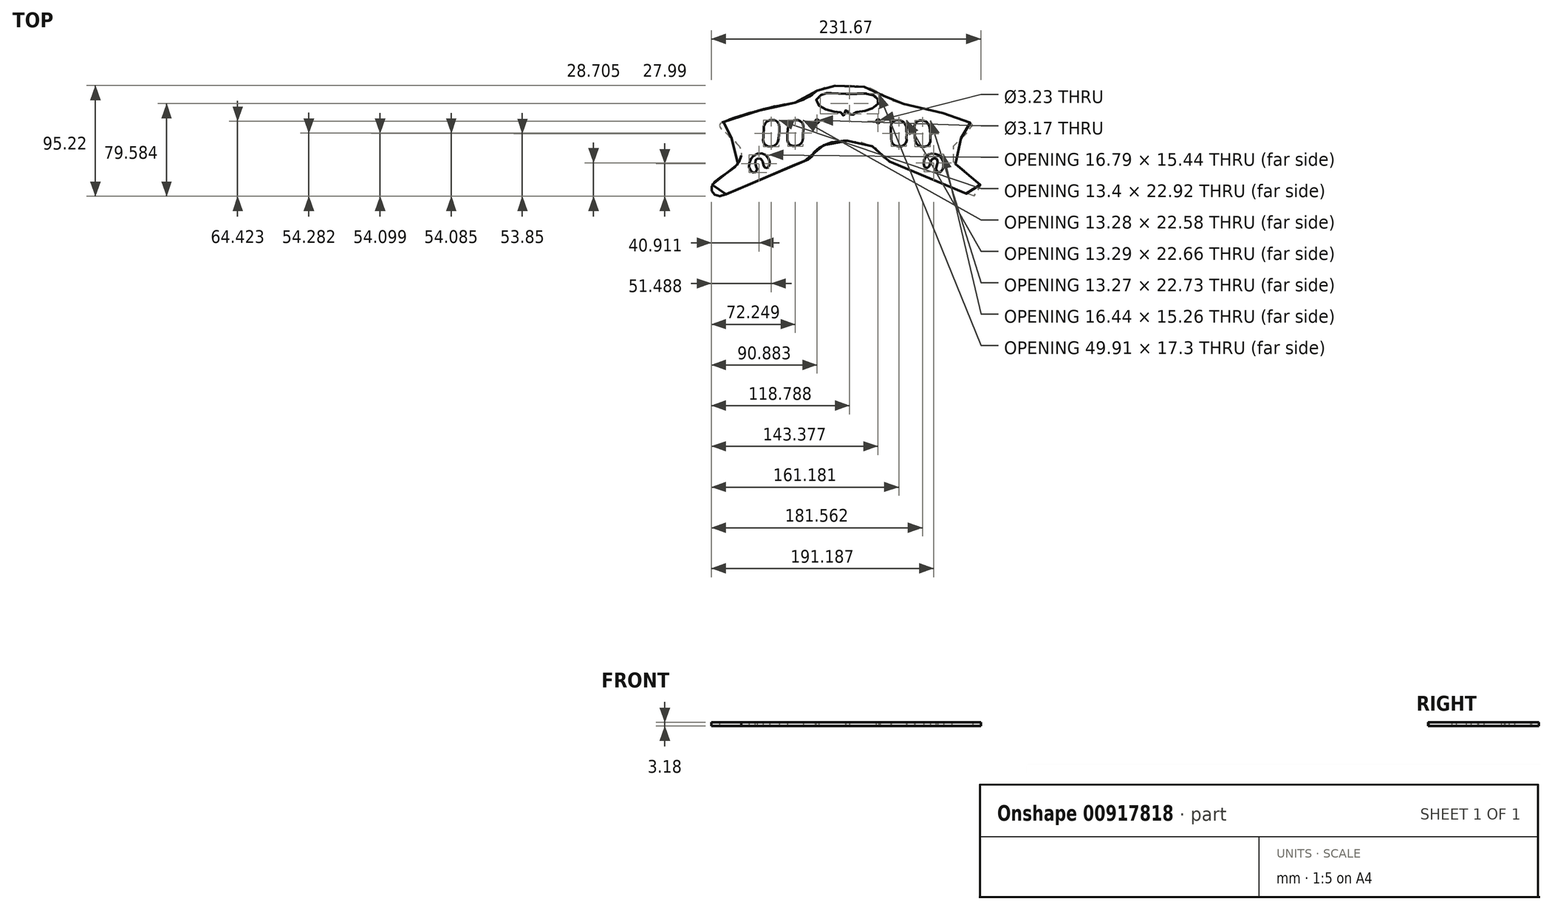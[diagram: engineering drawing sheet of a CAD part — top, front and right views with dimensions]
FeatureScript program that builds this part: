
annotation { "Feature Type Name" : "Feature", "Feature Type Description" : "" }
export const myFeature = defineFeature(function(context is Context, id is Id, definition is map)
    precondition{}
    {
        {
            var Q0;
            Q0=qCreatedBy(makeId("Top.planeOp"),FACE);
            var sketch = newSketch(context, id + "F0", { "sketchPlane" : qUnion([Q0])});
            skFitSpline(sketch, "E0", {"points": [v(0, -14.2) * mm, v(3.4, -14.29) * mm, v(7.2, -14.54) * mm, v(11.16, -15.12) * mm, v(15.2, -16.3) * mm, v(19.09, -17.8) * mm, v(22.72, -19.58) * mm, v(25.84, -21.68) * mm, v(28.12, -24.3) * mm, v(29.39, -26.82) * mm, v(30.57, -28.59) * mm, v(32.68, -30.36) * mm, v(36.14, -31.95) * mm, v(42.3, -34.56) * mm, v(100.55, -58.96) * mm, v(103.89, -60.5) * mm, v(106.63, -61.46) * mm, v(109.85, -61.22) * mm, v(112.23, -59.9) * mm, v(114.14, -57.16) * mm, v(114.5, -53.82) * mm, v(113.65, -50.84) * mm, v(111.5, -48.45) * mm, v(104.94, -43.46) * mm, v(98.14, -38.58) * mm, v(93.36, -34.89) * mm, v(90.61, -31.07) * mm, v(89.53, -25.7) * mm, v(90.24, -20.46) * mm, v(92.98, -16.17) * mm, v(97.5, -12.1) * mm, v(101.44, -8.64) * mm, v(104.36, -6.47) * mm, v(106.46, -4.36) * mm, v(107.76, -2.25) * mm, v(107.66, -0.65) * mm, v(106.94, 0.6) * mm, v(105.47, 1.38) * mm, v(100.68, 3.14) * mm, v(97.2, 4.45) * mm, v(92.2, 6.34) * mm, v(87.71, 7.9) * mm, v(81.83, 9.6) * mm, v(75.58, 11.3) * mm, v(64.24, 14.18) * mm, v(52.5, 16.58) * mm, v(46.47, 17.75) * mm, v(45.09, 18.07) * mm, v(43.7, 18.47) * mm, v(41.2, 19.28) * mm, v(39.02, 20.1) * mm, v(37.08, 20.98) * mm, v(33.1, 23.24) * mm, v(29.84, 25.36) * mm, v(27.98, 26.84) * mm, v(26.52, 27.9) * mm, v(24.06, 29.17) * mm, v(22.03, 30.03) * mm, v(20.12, 30.69) * mm, v(17.2, 31.51) * mm, v(11.82, 32.5) * mm, v(6.71, 33.13) * mm, v(2.74, 33.34) * mm, v(-2.5, 33.33) * mm, v(-7.82, 33.18) * mm, v(-13.13, 32.82) * mm, v(-17.7, 32.12) * mm, v(-18.63, 31.91) * mm, v(-20.71, 31.4) * mm, v(-22.17, 30.9) * mm, v(-23.05, 30.46) * mm, v(-23.92, 30.08) * mm, v(-24.74, 29.68) * mm, v(-25.56, 29.15) * mm, v(-27.13, 28.18) * mm, v(-30.04, 25.87) * mm, v(-33.07, 23.84) * mm, v(-36.76, 21.93) * mm, v(-40.93, 20.14) * mm, v(-45.22, 18.7) * mm, v(-49.6, 17.79) * mm, v(-56.82, 16.47) * mm, v(-65.34, 14.66) * mm, v(-74.97, 12.24) * mm, v(-83.09, 10.02) * mm, v(-90.5, 7.7) * mm, v(-98.82, 4.99) * mm, v(-106.54, 1.97) * mm, v(-108.42, 1.28) * mm, v(-109.55, 0.26) * mm, v(-109.97, -0.77) * mm, v(-109.83, -2) * mm, v(-109.01, -3.5) * mm, v(-107.74, -4.56) * mm, v(-101.42, -10.52) * mm, v(-95.69, -16) * mm, v(-92.46, -20.04) * mm, v(-91.39, -24.45) * mm, v(-91.74, -28.63) * mm, v(-93.64, -33.04) * mm, v(-97.8, -37.46) * mm, v(-104.03, -41.95) * mm, v(-110.55, -46.63) * mm, v(-114.94, -50.11) * mm, v(-116.78, -53.02) * mm, v(-117.13, -55.3) * mm, v(-116.63, -57.84) * mm, v(-115, -60.04) * mm, v(-112.23, -61.6) * mm, v(-109.11, -61.8) * mm, v(-105.43, -60.52) * mm, v(-47.82, -36.04) * mm, v(-37.57, -31.73) * mm, v(-33.87, -30.18) * mm, v(-31.73, -28.87) * mm, v(-30.06, -26.48) * mm, v(-28.28, -23.61) * mm, v(-25.06, -20.63) * mm, v(-20.18, -17.88) * mm, v(-15.05, -15.85) * mm, v(-11.91, -15.09) * mm, v(-7.78, -14.62) * mm, v(-4.07, -14.23) * mm, v(-2.34, -14.06) * mm, v(0, -14.2) * mm]});
            skSolve(sketch);
        }
        {
            var Q0;
            Q0=makeQuery(id+"F0.imprint","IMPRINT",FACE,{"disambiguationData":[TD([[makeQuery(id+"F0.imprint","IMPRINT",EDGE,{"derivedFrom":sQuery(id+"F0.wireOp",EDGE,"E0")}),1.0]])]});
            extrude(context, id + "F1", {"entities" : qUnion([Q0]), "depth" : 3.17 * mm, "offsetDistance" : 25.4 * mm});
        }
        {
            var Q0;
            Q0=qCreatedBy(makeId("Top.planeOp"),FACE);
            var sketch = newSketch(context, id + "F2", { "sketchPlane" : qUnion([Q0])});
            skPoint(sketch, "E1.109.internal.snap0", {"position": v(0, 0) * mm});
            skFitSpline(sketch, "E2", {"points": [v(1.7, 9.07) * mm, v(2.12, 8.1) * mm, v(2.7, 7.77) * mm, v(3.33, 7.63) * mm, v(4.06, 7.84) * mm, v(4.58, 8.43) * mm, v(4.99, 9.28) * mm, v(5.55, 9.97) * mm, v(6.6, 10.37) * mm, v(7.77, 10.51) * mm, v(9.9, 10.66) * mm, v(12.98, 11.1) * mm, v(16.14, 11.8) * mm, v(18.61, 12.48) * mm, v(20.55, 13.2) * mm, v(22.7, 14.39) * mm, v(24.76, 15.65) * mm, v(25.9, 17) * mm, v(26.5, 17.95) * mm, v(26.71, 18.94) * mm, v(26.71, 19.9) * mm, v(26.5, 20.97) * mm, v(26.1, 21.62) * mm, v(25.52, 22.58) * mm, v(24.32, 23.65) * mm, v(22.76, 24.6) * mm, v(21.24, 25.27) * mm, v(19.76, 25.73) * mm, v(17.74, 26.2) * mm, v(15.7, 26.32) * mm, v(14.34, 26.36) * mm, v(12.5, 26.38) * mm, v(10.67, 26.35) * mm, v(8.28, 26.3) * mm, v(6.2, 26.22) * mm, v(3.22, 26.13) * mm, v(2.08, 26.17) * mm, v(-0.1, 26.18) * mm, v(-1.68, 26.26) * mm, v(-3.52, 26.21) * mm, v(-5.8, 26.3) * mm, v(-8.42, 26.46) * mm, v(-10.48, 26.6) * mm, v(-12.55, 26.72) * mm, v(-13.95, 26.76) * mm, v(-15.43, 26.87) * mm, v(-16.38, 26.87) * mm, v(-17.15, 26.84) * mm, v(-17.96, 26.72) * mm, v(-19, 26.54) * mm, v(-19.87, 26.32) * mm, v(-20.96, 25.94) * mm, v(-22.52, 25.3) * mm, v(-24.33, 24.25) * mm, v(-25.94, 22.96) * mm, v(-27.03, 20.95) * mm, v(-26.98, 19.44) * mm, v(-26.13, 17.59) * mm, v(-24.83, 16.19) * mm, v(-23.17, 14.93) * mm, v(-21.27, 13.78) * mm, v(-18.76, 12.68) * mm, v(-16, 11.87) * mm, v(-13.15, 11.27) * mm, v(-10.14, 10.87) * mm, v(-7.83, 10.67) * mm, v(-6.53, 10.47) * mm, v(-5.87, 10.14) * mm, v(-5.3, 9.48) * mm, v(-4.82, 8.55) * mm, v(-4.57, 8.07) * mm, v(-4.06, 7.65) * mm, v(-3.15, 7.48) * mm, v(-2.2, 7.97) * mm, v(-1.7, 8.98) * mm, v(-1.7, 12.06) * mm, v(-1.5, 12.24) * mm, v(1.57, 12.24) * mm, v(1.7, 12.08) * mm, v(1.7, 9.07) * mm]});
            skFitSpline(sketch, "E3", {"points": [v(-77.28, -29.5) * mm, v(-75.85, -29.17) * mm, v(-74.7, -29.62) * mm, v(-73.74, -30.42) * mm, v(-73.02, -31.88) * mm, v(-72.51, -33.82) * mm, v(-72.13, -35.13) * mm, v(-71.77, -36.2) * mm, v(-71.32, -37.04) * mm, v(-70.76, -37.55) * mm, v(-69.83, -37.7) * mm, v(-68.76, -37.4) * mm, v(-67.95, -36.65) * mm, v(-67.27, -35.1) * mm, v(-67.03, -32.87) * mm, v(-67.45, -30.57) * mm, v(-68.43, -28.46) * mm, v(-70.1, -26.7) * mm, v(-72.13, -25.54) * mm, v(-74.45, -25) * mm, v(-76.84, -25.2) * mm, v(-79.2, -26.1) * mm, v(-81.19, -27.5) * mm, v(-82.74, -29.23) * mm, v(-83.96, -31.4) * mm, v(-84.53, -33.55) * mm, v(-84.62, -35.73) * mm, v(-84.35, -37.58) * mm, v(-83.45, -39.37) * mm, v(-82.44, -40.74) * mm, v(-81.49, -41.45) * mm, v(-80.26, -41.57) * mm, v(-79.2, -41.25) * mm, v(-78.33, -40.35) * mm, v(-77.9, -39.28) * mm, v(-77.9, -38.17) * mm, v(-78.3, -36.71) * mm, v(-78.9, -35.07) * mm, v(-79.25, -33.67) * mm, v(-79.49, -32.42) * mm, v(-79.25, -31.32) * mm, v(-78.66, -30.3) * mm, v(-77.9, -29.77) * mm, v(-77.28, -29.5) * mm]});
            skFitSpline(sketch, "E4", {"points": [v(-64.94, 3.7) * mm, v(-63.1, 3.7) * mm, v(-61.1, 2.8) * mm, v(-59.59, 1.24) * mm, v(-58.88, -1.03) * mm, v(-58.78, -4.54) * mm, v(-58.93, -7.9) * mm, v(-59.21, -11.73) * mm, v(-59.73, -14.57) * mm, v(-60.73, -16.37) * mm, v(-62.33, -17.93) * mm, v(-64.32, -18.92) * mm, v(-66.92, -19.25) * mm, v(-69.38, -18.54) * mm, v(-70.85, -17.5) * mm, v(-71.99, -16.08) * mm, v(-72.46, -14.57) * mm, v(-72.46, -11.82) * mm, v(-72.32, -8.51) * mm, v(-72.18, -5.39) * mm, v(-71.94, -2.26) * mm, v(-71.47, -0.51) * mm, v(-70.33, 1.43) * mm, v(-68.25, 3.08) * mm, v(-66.26, 3.56) * mm, v(-64.94, 3.7) * mm]});
            skFitSpline(sketch, "E5", {"points": [v(-44.82, 3.7) * mm, v(-42.88, 3.7) * mm, v(-41, 3.1) * mm, v(-39.05, 1.63) * mm, v(-38.06, -0.64) * mm, v(-38, -4.71) * mm, v(-38.34, -9.02) * mm, v(-38.48, -13.37) * mm, v(-39.29, -15.5) * mm, v(-40.85, -17.25) * mm, v(-43.12, -18.44) * mm, v(-46, -18.86) * mm, v(-48.66, -18.15) * mm, v(-50.45, -16.78) * mm, v(-51.5, -15.03) * mm, v(-51.69, -13.52) * mm, v(-51.73, -9.26) * mm, v(-51.4, -5.04) * mm, v(-51.16, -2.06) * mm, v(-50.5, -0.45) * mm, v(-49.56, 1.4) * mm, v(-47.57, 2.76) * mm, v(-45.91, 3.57) * mm, v(-44.82, 3.7) * mm]});
            skFitSpline(sketch, "E6", {"points": [v(43.58, 3.56) * mm, v(45.37, 3.31) * mm, v(47.3, 2.51) * mm, v(48.94, 1.14) * mm, v(50.1, -0.7) * mm, v(50.55, -2.43) * mm, v(50.64, -5.89) * mm, v(50.73, -9) * mm, v(50.68, -12.4) * mm, v(50.72, -13.76) * mm, v(50.55, -15.2) * mm, v(49.68, -16.8) * mm, v(47.96, -18.29) * mm, v(45.71, -19.02) * mm, v(42.96, -19.02) * mm, v(40.65, -18.17) * mm, v(39.07, -16.94) * mm, v(38.14, -15.44) * mm, v(37.53, -13.73) * mm, v(37.41, -11.05) * mm, v(37.38, -6.6) * mm, v(37.3, -3.78) * mm, v(37.27, -0.87) * mm, v(37.94, 1.04) * mm, v(39.5, 2.55) * mm, v(41.24, 3.36) * mm, v(43.58, 3.56) * mm]});
            skFitSpline(sketch, "E7", {"points": [v(63.66, 3.35) * mm, v(65.41, 3.08) * mm, v(67.11, 2.48) * mm, v(68.91, 1.15) * mm, v(70.26, -0.88) * mm, v(70.76, -3.9) * mm, v(71.05, -7.21) * mm, v(71.22, -11.73) * mm, v(71.22, -15.1) * mm, v(70.54, -16.67) * mm, v(69.2, -18.3) * mm, v(66.83, -19.26) * mm, v(64.07, -19.31) * mm, v(61.7, -18.58) * mm, v(59.8, -17.12) * mm, v(58.56, -15.26) * mm, v(57.88, -12.78) * mm, v(57.83, -7.94) * mm, v(57.66, -3.72) * mm, v(57.63, -1.35) * mm, v(57.96, 0.3) * mm, v(58.93, 1.85) * mm, v(60.99, 3.08) * mm, v(62.57, 3.36) * mm, v(63.66, 3.35) * mm]});
            skFitSpline(sketch, "E8", {"points": [v(75.6, -25.53) * mm, v(77.25, -26.1) * mm, v(78.96, -27.2) * mm, v(80.7, -29) * mm, v(82.02, -31.12) * mm, v(82.65, -33.36) * mm, v(82.65, -36.26) * mm, v(81.96, -38.41) * mm, v(80.92, -40.05) * mm, v(79.62, -41.32) * mm, v(78.23, -41.54) * mm, v(76.75, -40.62) * mm, v(76.02, -39.4) * mm, v(75.99, -37.94) * mm, v(76.5, -36.14) * mm, v(77.32, -33.7) * mm, v(77.6, -32.16) * mm, v(77.32, -30.83) * mm, v(76.59, -29.79) * mm, v(75.48, -29.32) * mm, v(73.8, -29.25) * mm, v(72.55, -29.95) * mm, v(71.66, -31.24) * mm, v(70.97, -33.36) * mm, v(70.4, -35.25) * mm, v(69.99, -36.52) * mm, v(69.2, -37.37) * mm, v(67.75, -37.69) * mm, v(66.67, -37.18) * mm, v(65.72, -35.76) * mm, v(65.5, -34.05) * mm, v(65.53, -32.28) * mm, v(65.98, -30.36) * mm, v(66.77, -28.72) * mm, v(68.03, -27.07) * mm, v(69.77, -25.9) * mm, v(71.76, -25.34) * mm, v(73.94, -25.24) * mm, v(75.6, -25.53) * mm]});
            skLineSegment(sketch, "E9.bottom", {"start": v(26.25, 2.56) * mm, "end": v(-26.25, 2.56) * mm, "construction": true});
            skLineSegment(sketch, "E9.top", {"start": v(26.25, -19.24) * mm, "end": v(-26.25, -19.24) * mm, "construction": true});
            skLineSegment(sketch, "E9.left", {"start": v(26.25, 2.56) * mm, "end": v(26.25, -19.24) * mm, "construction": true});
            skLineSegment(sketch, "E9.right", {"start": v(-26.25, 2.56) * mm, "end": v(-26.25, -19.24) * mm, "construction": true});
            skPoint(sketch, "E9.middle", {"position": v(0, -8.34) * mm});
            skCircle(sketch, "E10", {"center": v(26.25, 2.56) * mm, "radius": 1.61 * mm});
            skCircle(sketch, "E11", {"center": v(-26.25, 2.56) * mm, "radius": 1.59 * mm});
            skSolve(sketch);
        }
        {
            var Q0;
            Q0 = qSketchRegion(id + "F2", true);
            extrude(context, id + "F3", {"entities" : qUnion([Q0]), "operationType" : NewBodyOperationType.REMOVE, "depth" : 25.4 * mm, "offsetDistance" : 25.4 * mm});
        }
    });
